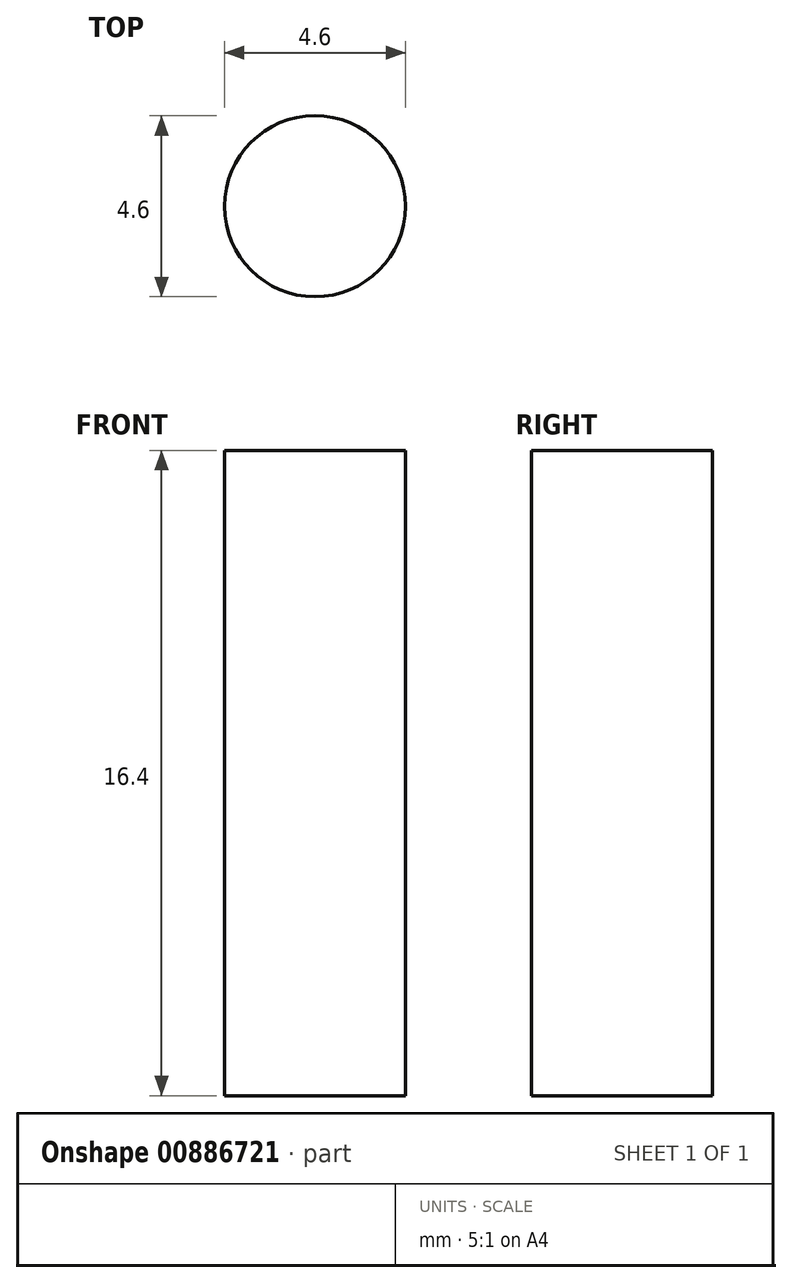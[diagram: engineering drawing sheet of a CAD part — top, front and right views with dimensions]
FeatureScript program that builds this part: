
annotation { "Feature Type Name" : "Feature", "Feature Type Description" : "" }
export const myFeature = defineFeature(function(context is Context, id is Id, definition is map)
    precondition{}
    {
        {
            var Q0;
            Q0=qCreatedBy(makeId("Top.planeOp"),FACE);
            var sketch = newSketch(context, id + "F0", { "sketchPlane" : qUnion([Q0])});
            skCircle(sketch, "E0", {"center": v(0, 0) * mm, "radius": 2.3 * mm});
            skSolve(sketch);
        }
        {
            var Q0;
            Q0 = qSketchRegion(id + "F0", true);
            extrude(context, id + "F1", {"entities" : qUnion([Q0]), "depth" : 16.4 * mm, "offsetDistance" : 25 * mm});
        }
    });
